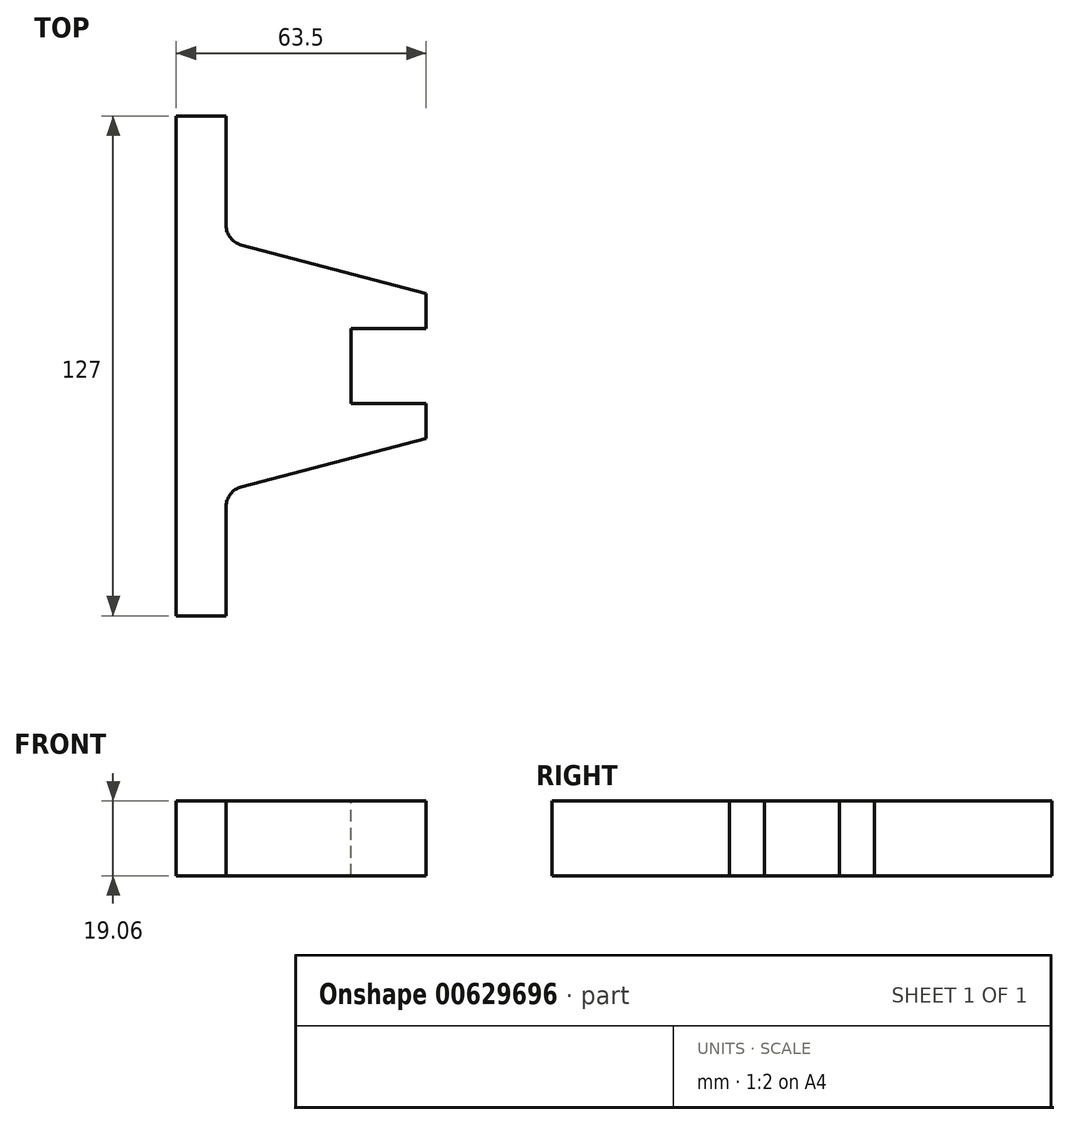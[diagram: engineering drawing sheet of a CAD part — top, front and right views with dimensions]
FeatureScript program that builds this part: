
annotation { "Feature Type Name" : "Feature", "Feature Type Description" : "" }
export const myFeature = defineFeature(function(context is Context, id is Id, definition is map)
    precondition{}
    {
        {
            var Q0;
            Q0=qCreatedBy(makeId("Top.planeOp"),FACE);
            var sketch = newSketch(context, id + "F0", { "sketchPlane" : qUnion([Q0])});
            skLineSegment(sketch, "E0.bottom", {"start": v(-31.75, 63.5) * mm, "end": v(31.75, 63.5) * mm});
            skLineSegment(sketch, "E0.top", {"start": v(-31.75, -63.5) * mm, "end": v(31.75, -63.5) * mm});
            skLineSegment(sketch, "E0.left", {"start": v(-31.75, 63.5) * mm, "end": v(-31.75, -63.5) * mm});
            skLineSegment(sketch, "E0.right", {"start": v(31.75, 63.5) * mm, "end": v(31.75, -63.5) * mm});
            skLineSegment(sketch, "E1", {"start": v(31.75, 63.5) * mm, "end": v(-31.75, -63.5) * mm, "construction": true});
            skSolve(sketch);
        }
        {
            var Q0;
            Q0=qSketchRegion(id+"F0",true);
            extrude(context, id + "F1", {"entities" : qUnion([Q0]), "endBound" : BoundingType.SYMMETRIC, "depth" : 19.05 * mm});
        }
        {
            var Q0;
            Q0=makeQuery(id+"F1.opExtrude","CAP_FACE",FACE,{"disambiguationData":[OSD([sQuery(id+"F0.wireOp",EDGE,"E0.bottom"),sQuery(id+"F0.wireOp",EDGE,"E0.top"),sQuery(id+"F0.wireOp",EDGE,"E0.left"),sQuery(id+"F0.wireOp",EDGE,"E0.right")])],"isStart":false});
            var sketch = newSketch(context, id + "F2", { "sketchPlane" : qUnion([Q0])});
            skLineSegment(sketch, "E2", {"start": v(0, 0) * mm, "end": v(31.75, 0) * mm, "construction": true});
            skLineSegment(sketch, "E3.bottom", {"start": v(31.75, 9.53) * mm, "end": v(12.7, 9.53) * mm});
            skLineSegment(sketch, "E3.top", {"start": v(31.75, -9.53) * mm, "end": v(12.7, -9.53) * mm});
            skLineSegment(sketch, "E3.left", {"start": v(31.75, 9.53) * mm, "end": v(31.75, -9.53) * mm});
            skLineSegment(sketch, "E3.right", {"start": v(12.7, 9.53) * mm, "end": v(12.7, -9.53) * mm});
            skSolve(sketch);
        }
        {
            var Q0;
            Q0=qSketchRegion(id+"F2",true);
            extrude(context, id + "F3", {"entities" : qUnion([Q0]), "operationType" : NewBodyOperationType.REMOVE, "endBound" : BoundingType.THROUGH_ALL, "oppositeDirection" : true, "depth" : 25.4 * mm});
        }
        {
            var Q0;
            Q0=makeQuery(id+"F1.opExtrude","CAP_FACE",FACE,{"disambiguationData":[OSD([sQuery(id+"F0.wireOp",EDGE,"E0.bottom"),sQuery(id+"F0.wireOp",EDGE,"E0.top"),sQuery(id+"F0.wireOp",EDGE,"E0.left"),sQuery(id+"F0.wireOp",EDGE,"E0.right")])],"isStart":false});
            var sketch = newSketch(context, id + "F4", { "sketchPlane" : qUnion([Q0])});
            skLineSegment(sketch, "E4", {"start": v(-19.05, 63.5) * mm, "end": v(-19.05, 31.75) * mm});
            skLineSegment(sketch, "E5", {"start": v(-19.05, 31.75) * mm, "end": v(31.75, 18.41) * mm});
            skLineSegment(sketch, "E6", {"start": v(-19.05, -31.75) * mm, "end": v(31.75, -18.42) * mm});
            skLineSegment(sketch, "E7.trimOffspring", {"start": v(-19.05, -31.75) * mm, "end": v(-19.05, -63.5) * mm});
            skLineSegment(sketch, "E8", {"start": v(-19.05, 31.75) * mm, "end": v(-19.05, -31.75) * mm, "construction": true});
            skLineSegment(sketch, "E9", {"start": v(31.75, 18.41) * mm, "end": v(31.75, -18.41) * mm, "construction": true});
            skLineSegment(sketch, "E10", {"start": v(31.75, 0) * mm, "end": v(-19.05, 0) * mm, "construction": true});
            skLineSegment(sketch, "E11", {"start": v(-19.05, 63.5) * mm, "end": v(31.75, 63.5) * mm});
            skLineSegment(sketch, "E12", {"start": v(31.75, 63.5) * mm, "end": v(31.75, 18.42) * mm});
            skLineSegment(sketch, "E13", {"start": v(-19.05, -63.5) * mm, "end": v(31.75, -63.5) * mm});
            skLineSegment(sketch, "E14", {"start": v(31.75, -63.5) * mm, "end": v(31.75, -18.42) * mm});
            skSolve(sketch);
        }
        {
            var Q0;
            Q0=qSketchRegion(id+"F4",true);
            extrude(context, id + "F5", {"entities" : qUnion([Q0]), "operationType" : NewBodyOperationType.REMOVE, "endBound" : BoundingType.THROUGH_ALL, "oppositeDirection" : true, "depth" : 25.4 * mm});
        }
        {
            var Q0;
            Q0=makeQuery(id+"F5.boolean.opBoolean","COPY",EDGE,{"derivedFrom":makeQuery(id+"F5.opExtrude","SWEPT_EDGE",EDGE,{"disambiguationData":[OSD([sQuery(id+"F4.wireOp",EDGE,"E6"),sQuery(id+"F4.wireOp",EDGE,"E7.trimOffspring")])]})});
            var Q1;
            Q1=makeQuery(id+"F5.boolean.opBoolean","COPY",EDGE,{"derivedFrom":makeQuery(id+"F5.opExtrude","SWEPT_EDGE",EDGE,{"disambiguationData":[OSD([sQuery(id+"F0.wireOp",EDGE,"E0.top"),sQuery(id+"F4.wireOp",EDGE,"E7.trimOffspring"),sQuery(id+"F4.wireOp",EDGE,"E13")])]})});
            var Q2;
            Q2=makeQuery(id+"F5.boolean.opBoolean","COPY",EDGE,{"derivedFrom":makeQuery(id+"F5.opExtrude","SWEPT_EDGE",EDGE,{"disambiguationData":[OSD([sQuery(id+"F0.wireOp",EDGE,"E0.right"),sQuery(id+"F4.wireOp",EDGE,"E6"),sQuery(id+"F4.wireOp",EDGE,"E14")])]})});
            var Q3;
            Q3=makeQuery(id+"F5.boolean.opBoolean","COPY",EDGE,{"derivedFrom":makeQuery(id+"F5.opExtrude","SWEPT_EDGE",EDGE,{"disambiguationData":[OSD([sQuery(id+"F0.wireOp",EDGE,"E0.right"),sQuery(id+"F4.wireOp",EDGE,"E5"),sQuery(id+"F4.wireOp",EDGE,"E12")])]})});
            var Q4;
            Q4=makeQuery(id+"F5.boolean.opBoolean","COPY",EDGE,{"derivedFrom":makeQuery(id+"F5.opExtrude","SWEPT_EDGE",EDGE,{"disambiguationData":[OSD([sQuery(id+"F4.wireOp",EDGE,"E4"),sQuery(id+"F4.wireOp",EDGE,"E5")])]})});
            var Q5;
            Q5=makeQuery(id+"F5.boolean.opBoolean","COPY",EDGE,{"derivedFrom":makeQuery(id+"F5.opExtrude","SWEPT_EDGE",EDGE,{"disambiguationData":[OSD([sQuery(id+"F0.wireOp",EDGE,"E0.bottom"),sQuery(id+"F4.wireOp",EDGE,"E4"),sQuery(id+"F4.wireOp",EDGE,"E11")])]})});
            fillet(context, id + "F6", {"entities" : qUnion([Q0, Q1, Q2, Q3, Q4, Q5]), "radius" : 5.08 * mm, "tangentPropagation" : true, "allowEdgeOverflow" : false});
        }
    });
